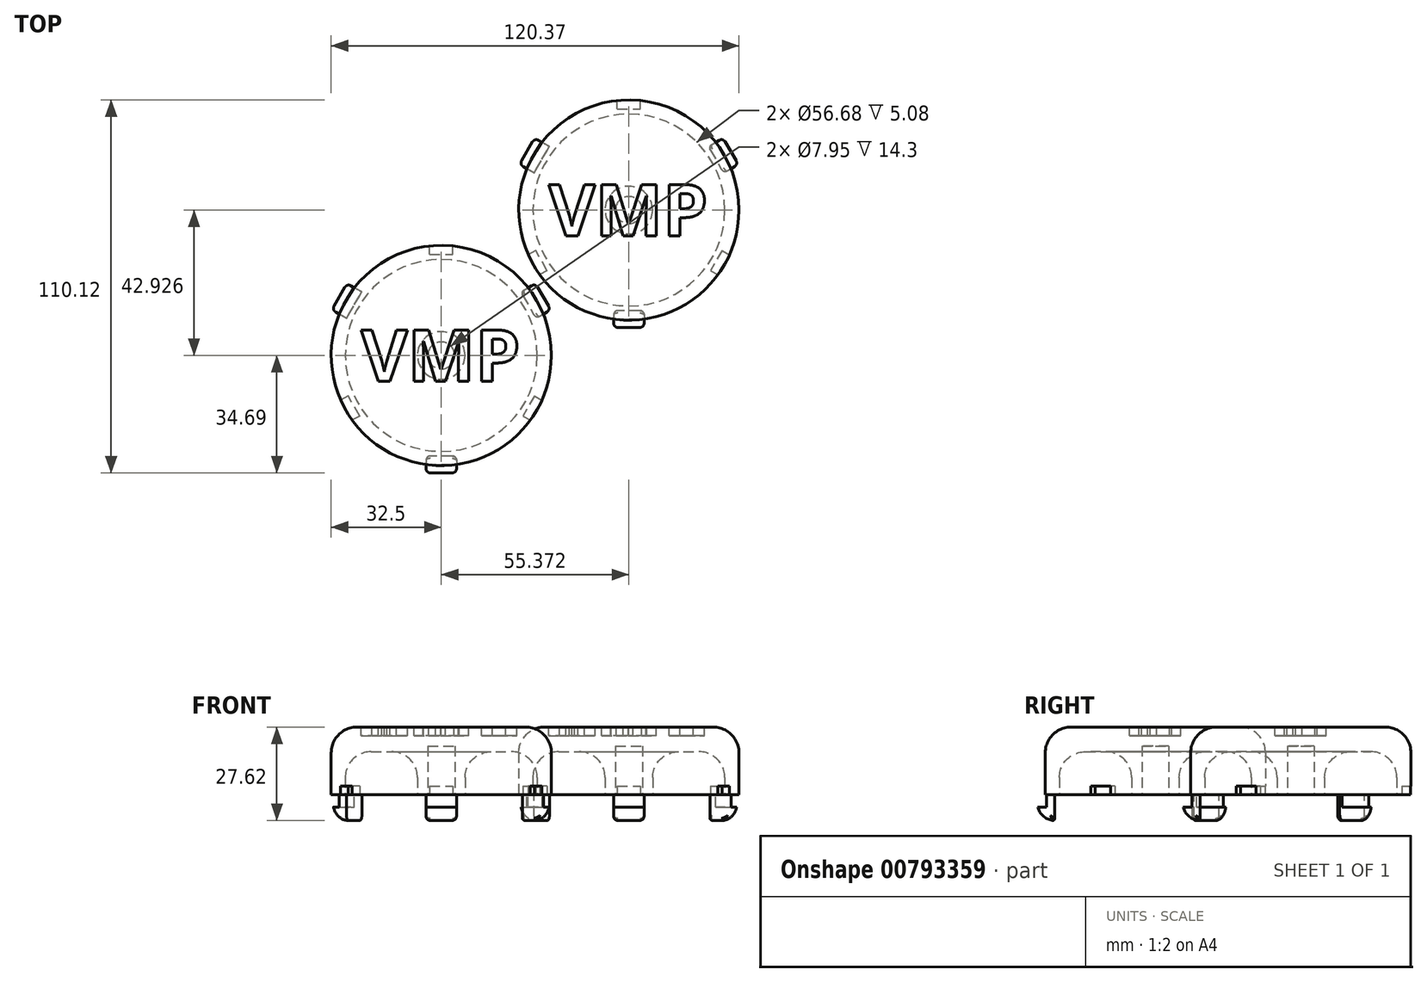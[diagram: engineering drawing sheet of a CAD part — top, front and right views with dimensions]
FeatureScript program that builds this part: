
annotation { "Feature Type Name" : "Feature", "Feature Type Description" : "" }
export const myFeature = defineFeature(function(context is Context, id is Id, definition is map)
    precondition{}
    {
        {
            var Q0;
            Q0=qCreatedBy(makeId("Top.planeOp"),FACE);
            var sketch = newSketch(context, id + "F0", { "sketchPlane" : qUnion([Q0])});
            skCircle(sketch, "E0", {"center": v(0, 0) * mm, "radius": 32.5 * mm});
            skSolve(sketch);
        }
        {
            var Q0;
            Q0=makeQuery(id+"F0.imprint","IMPRINT",FACE,{"disambiguationData":[TD([[makeQuery(id+"F0.imprint","IMPRINT",EDGE,{"derivedFrom":sQuery(id+"F0.wireOp",EDGE,"E0")}),1.0]])]});
            extrude(context, id + "F1", {"entities" : qUnion([Q0]), "depth" : 20 * mm, "offsetDistance" : 25.4 * mm});
        }
        {
            var Q0;
            Q0=makeQuery(id+"F1.opExtrude","CAP_FACE",FACE,{"disambiguationData":[OSD([sQuery(id+"F0.wireOp",EDGE,"E0")])],"isStart":false});
            fillet(context, id + "F2", {"entities" : qUnion([Q0]), "radius" : 7.62 * mm, "tangentPropagation" : true, "allowEdgeOverflow" : false});
        }
        {
            var Q0;
            Q0=makeQuery(id+"F1.opExtrude","CAP_FACE",FACE,{"disambiguationData":[OSD([sQuery(id+"F0.wireOp",EDGE,"E0")])],"isStart":true});
            var sketch = newSketch(context, id + "F3", { "sketchPlane" : qUnion([Q0])});
            skCircle(sketch, "E1", {"center": v(0, 0) * mm, "radius": 3.98 * mm});
            skSolve(sketch);
        }
        {
            var Q0;
            Q0=makeQuery(id+"F3.imprint","IMPRINT",FACE,{"disambiguationData":[TD([[makeQuery(id+"F3.imprint","IMPRINT",EDGE,{"derivedFrom":sQuery(id+"F3.wireOp",EDGE,"E1")}),1.0]])]});
            extrude(context, id + "F4", {"entities" : qUnion([Q0]), "operationType" : NewBodyOperationType.REMOVE, "oppositeDirection" : true, "depth" : 14.3 * mm, "offsetDistance" : 25.4 * mm});
        }
        {
            var Q0;
            Q0=makeQuery(id+"F1.opExtrude","CAP_FACE",FACE,{"disambiguationData":[OSD([sQuery(id+"F0.wireOp",EDGE,"E0")])],"isStart":true});
            var sketch = newSketch(context, id + "F5", { "sketchPlane" : qUnion([Q0])});
            skLineSegment(sketch, "E2.bottom", {"start": v(0, 29.69) * mm, "end": v(-4.5, 29.69) * mm});
            skLineSegment(sketch, "E2.top", {"start": v(0, 32.19) * mm, "end": v(-4.5, 32.19) * mm});
            skLineSegment(sketch, "E2.right", {"start": v(-4.5, 29.69) * mm, "end": v(-4.5, 32.19) * mm});
            skLineSegment(sketch, "E3.MirrorCS", {"start": v(0, 29.69) * mm, "end": v(4.5, 29.69) * mm});
            skLineSegment(sketch, "E4.MirrorCS", {"start": v(4.5, 29.69) * mm, "end": v(4.5, 32.19) * mm});
            skLineSegment(sketch, "E5.MirrorCS", {"start": v(0, 32.19) * mm, "end": v(4.5, 32.19) * mm});
            skLineSegment(sketch, "E6.1.0", {"start": v(-27.87, -16.1) * mm, "end": v(-30.12, -12.2) * mm});
            skLineSegment(sketch, "E6.1.1", {"start": v(-25.7, -14.84) * mm, "end": v(-27.96, -10.95) * mm});
            skLineSegment(sketch, "E6.1.2", {"start": v(-25.7, -14.84) * mm, "end": v(-23.46, -18.74) * mm});
            skLineSegment(sketch, "E6.1.3", {"start": v(-23.46, -18.74) * mm, "end": v(-25.62, -20) * mm});
            skLineSegment(sketch, "E6.1.4", {"start": v(-27.87, -16.1) * mm, "end": v(-25.62, -20) * mm});
            skLineSegment(sketch, "E6.1.5", {"start": v(-27.96, -10.95) * mm, "end": v(-30.12, -12.2) * mm});
            skLineSegment(sketch, "E6.2.0", {"start": v(27.87, -16.1) * mm, "end": v(25.62, -20) * mm});
            skLineSegment(sketch, "E6.2.1", {"start": v(25.7, -14.84) * mm, "end": v(23.46, -18.74) * mm});
            skLineSegment(sketch, "E6.2.2", {"start": v(25.7, -14.84) * mm, "end": v(27.96, -10.95) * mm});
            skLineSegment(sketch, "E6.2.3", {"start": v(27.96, -10.95) * mm, "end": v(30.12, -12.2) * mm});
            skLineSegment(sketch, "E6.2.4", {"start": v(27.87, -16.1) * mm, "end": v(30.12, -12.2) * mm});
            skLineSegment(sketch, "E6.2.5", {"start": v(23.46, -18.74) * mm, "end": v(25.62, -20) * mm});
            skPoint(sketch, "E6.center", {"position": v(0, 0) * mm});
            skSolve(sketch);
        }
        {
            var Q0;
            Q0=makeQuery(id+"F5.imprint","IMPRINT",FACE,{"disambiguationData":[TD([[makeQuery(id+"F5.imprint","IMPRINT",EDGE,{"derivedFrom":sQuery(id+"F5.wireOp",EDGE,"E2.bottom")}),-1.0]])]});
            var Q1;
            Q1=makeQuery(id+"F5.imprint","IMPRINT",FACE,{"disambiguationData":[TD([[makeQuery(id+"F5.imprint","IMPRINT",EDGE,{"derivedFrom":sQuery(id+"F5.wireOp",EDGE,"E6.2.0")}),-1.0]])]});
            var Q2;
            Q2=makeQuery(id+"F5.imprint","IMPRINT",FACE,{"disambiguationData":[TD([[makeQuery(id+"F5.imprint","IMPRINT",EDGE,{"derivedFrom":sQuery(id+"F5.wireOp",EDGE,"E6.1.0")}),-1.0]])]});
            extrude(context, id + "F6", {"entities" : qUnion([Q0, Q1, Q2]), "operationType" : NewBodyOperationType.ADD, "depth" : 7.62 * mm, "offsetDistance" : 25.4 * mm});
        }
        {
            var Q0;
            Q0=makeQuery(id+"F6.opExtrude","SWEPT_FACE",FACE,{"disambiguationData":[OSD([sQuery(id+"F5.wireOp",EDGE,"E6.1.0"),sQuery(id+"F5.wireOp",EDGE,"E6.1.4")])]});
            var sketch = newSketch(context, id + "F7", { "sketchPlane" : qUnion([Q0])});
            skLineSegment(sketch, "E7.bottom", {"start": v(4.5, -7.62) * mm, "end": v(-4.5, -7.62) * mm});
            skLineSegment(sketch, "E7.top", {"start": v(4.5, -3.62) * mm, "end": v(-4.5, -3.62) * mm});
            skLineSegment(sketch, "E7.left", {"start": v(4.5, -7.62) * mm, "end": v(4.5, -3.62) * mm});
            skLineSegment(sketch, "E7.right", {"start": v(-4.5, -7.62) * mm, "end": v(-4.5, -3.62) * mm});
            skSolve(sketch);
        }
        {
            var Q0;
            Q0=makeQuery(id+"F6.opExtrude","SWEPT_FACE",FACE,{"disambiguationData":[OSD([sQuery(id+"F5.wireOp",EDGE,"E6.2.0"),sQuery(id+"F5.wireOp",EDGE,"E6.2.4")])]});
            var sketch = newSketch(context, id + "F8", { "sketchPlane" : qUnion([Q0])});
            skLineSegment(sketch, "E8.bottom", {"start": v(4.5, -7.62) * mm, "end": v(-4.5, -7.62) * mm});
            skLineSegment(sketch, "E8.top", {"start": v(4.5, -3.62) * mm, "end": v(-4.5, -3.62) * mm});
            skLineSegment(sketch, "E8.left", {"start": v(4.5, -7.62) * mm, "end": v(4.5, -3.62) * mm});
            skLineSegment(sketch, "E8.right", {"start": v(-4.5, -7.62) * mm, "end": v(-4.5, -3.62) * mm});
            skSolve(sketch);
        }
        {
            var Q0;
            Q0=makeQuery(id+"F6.opExtrude","SWEPT_FACE",FACE,{"disambiguationData":[OSD([sQuery(id+"F5.wireOp",EDGE,"E2.top"),sQuery(id+"F5.wireOp",EDGE,"E5.MirrorCS")])]});
            var sketch = newSketch(context, id + "F9", { "sketchPlane" : qUnion([Q0])});
            skLineSegment(sketch, "E9.bottom", {"start": v(-4.5, -7.62) * mm, "end": v(4.5, -7.62) * mm});
            skLineSegment(sketch, "E9.top", {"start": v(-4.5, -3.62) * mm, "end": v(4.5, -3.62) * mm});
            skLineSegment(sketch, "E9.left", {"start": v(-4.5, -7.62) * mm, "end": v(-4.5, -3.62) * mm});
            skLineSegment(sketch, "E9.right", {"start": v(4.5, -7.62) * mm, "end": v(4.5, -3.62) * mm});
            skSolve(sketch);
        }
        {
            var Q0;
            Q0=makeQuery(id+"F9.imprint","IMPRINT",FACE,{"disambiguationData":[TD([[makeQuery(id+"F9.imprint","IMPRINT",EDGE,{"derivedFrom":sQuery(id+"F9.wireOp",EDGE,"E9.bottom")}),1.0]])]});
            extrude(context, id + "F10", {"entities" : qUnion([Q0]), "operationType" : NewBodyOperationType.ADD, "depth" : 2.5 * mm, "offsetDistance" : 25.4 * mm});
        }
        {
            var Q0;
            Q0=makeQuery(id+"F7.imprint","IMPRINT",FACE,{"disambiguationData":[TD([[makeQuery(id+"F7.imprint","IMPRINT",EDGE,{"derivedFrom":sQuery(id+"F7.wireOp",EDGE,"E7.bottom")}),1.0]])]});
            extrude(context, id + "F11", {"entities" : qUnion([Q0]), "operationType" : NewBodyOperationType.ADD, "depth" : 2.5 * mm, "offsetDistance" : 25.4 * mm});
        }
        {
            var Q0;
            Q0=makeQuery(id+"F8.imprint","IMPRINT",FACE,{"disambiguationData":[TD([[makeQuery(id+"F8.imprint","IMPRINT",EDGE,{"derivedFrom":sQuery(id+"F8.wireOp",EDGE,"E8.bottom")}),1.0]])]});
            extrude(context, id + "F12", {"entities" : qUnion([Q0]), "operationType" : NewBodyOperationType.ADD, "depth" : 2.5 * mm, "offsetDistance" : 25.4 * mm});
        }
        {
            var Q0;
            Q0=makeQuery(id+"F12.opExtrude","CAP_EDGE",EDGE,{"disambiguationData":[OSD([sQuery(id+"F8.wireOp",EDGE,"E8.bottom")])],"isStart":false});
            var Q1;
            Q1=makeQuery(id+"F10.opExtrude","CAP_EDGE",EDGE,{"disambiguationData":[OSD([sQuery(id+"F9.wireOp",EDGE,"E9.bottom")])],"isStart":false});
            var Q2;
            Q2=makeQuery(id+"F11.opExtrude","CAP_EDGE",EDGE,{"disambiguationData":[OSD([sQuery(id+"F7.wireOp",EDGE,"E7.bottom")])],"isStart":false});
            fillet(context, id + "F13", {"entities" : qUnion([Q0, Q1, Q2]), "radius" : 5.08 * mm, "tangentPropagation" : true, "allowEdgeOverflow" : false});
        }
        {
            var Q0;
            Q0=makeQuery(id+"F6.opExtrude","CAP_EDGE",EDGE,{"disambiguationData":[OSD([sQuery(id+"F5.wireOp",EDGE,"E2.bottom"),sQuery(id+"F5.wireOp",EDGE,"E3.MirrorCS")])],"isStart":false});
            var Q1;
            {var subQ0=sQuery(id+"F7.wireOp",EDGE,"E7.bottom");Q1=makeQuery(id+"F13.opFillet","BLEND_EDGE",EDGE,{"blendedFrom":[makeQuery(id+"F11.opExtrude","CAP_EDGE",EDGE,{"disambiguationData":[OSD([subQ0])],"isStart":false}),makeQuery(id+"F11.boolean.opBoolean","MERGE",FACE,{"derivedFrom":[makeQuery(id+"F6.opExtrude","CAP_FACE",FACE,{"disambiguationData":[OSD([sQuery(id+"F5.wireOp",EDGE,"E6.1.0"),sQuery(id+"F5.wireOp",EDGE,"E6.1.1"),sQuery(id+"F5.wireOp",EDGE,"E6.1.2"),sQuery(id+"F5.wireOp",EDGE,"E6.1.3"),sQuery(id+"F5.wireOp",EDGE,"E6.1.4"),sQuery(id+"F5.wireOp",EDGE,"E6.1.5")])],"isStart":false}),makeQuery(id+"F11.opExtrude","SWEPT_FACE",FACE,{"disambiguationData":[OSD([subQ0])]})]})],"blendedInto":[makeQuery(id+"F11.boolean.opBoolean","MERGE",FACE,{"derivedFrom":[makeQuery(id+"F6.opExtrude","CAP_FACE",FACE,{"disambiguationData":[OSD([sQuery(id+"F5.wireOp",EDGE,"E6.1.0"),sQuery(id+"F5.wireOp",EDGE,"E6.1.1"),sQuery(id+"F5.wireOp",EDGE,"E6.1.2"),sQuery(id+"F5.wireOp",EDGE,"E6.1.3"),sQuery(id+"F5.wireOp",EDGE,"E6.1.4"),sQuery(id+"F5.wireOp",EDGE,"E6.1.5")])],"isStart":false}),makeQuery(id+"F11.opExtrude","SWEPT_FACE",FACE,{"disambiguationData":[OSD([subQ0])]})]})]});}
            var Q2;
            Q2=makeQuery(id+"F6.opExtrude","CAP_EDGE",EDGE,{"disambiguationData":[OSD([sQuery(id+"F5.wireOp",EDGE,"E6.2.1"),sQuery(id+"F5.wireOp",EDGE,"E6.2.2")])],"isStart":false});
            fillet(context, id + "F14", {"entities" : qUnion([Q0, Q1, Q2]), "radius" : 0.64 * mm, "tangentPropagation" : true, "allowEdgeOverflow" : false});
        }
        {
            var Q0;
            Q0=makeQuery(id+"F13.opFillet","BLEND_EDGE",EDGE,{"blendedFrom":[makeQuery(id+"F11.opExtrude","CAP_EDGE",EDGE,{"disambiguationData":[OSD([sQuery(id+"F7.wireOp",EDGE,"E7.bottom")])],"isStart":false}),makeQuery(id+"F11.boolean.opBoolean","MERGE",FACE,{"derivedFrom":[makeQuery(id+"F6.opExtrude","SWEPT_FACE",FACE,{"disambiguationData":[OSD([sQuery(id+"F5.wireOp",EDGE,"E6.1.3")])]}),makeQuery(id+"F11.opExtrude","SWEPT_FACE",FACE,{"disambiguationData":[OSD([sQuery(id+"F7.wireOp",EDGE,"E7.right")])]})]})],"blendedInto":[makeQuery(id+"F11.boolean.opBoolean","MERGE",FACE,{"derivedFrom":[makeQuery(id+"F6.opExtrude","SWEPT_FACE",FACE,{"disambiguationData":[OSD([sQuery(id+"F5.wireOp",EDGE,"E6.1.3")])]}),makeQuery(id+"F11.opExtrude","SWEPT_FACE",FACE,{"disambiguationData":[OSD([sQuery(id+"F7.wireOp",EDGE,"E7.right")])]})]})]});
            var Q1;
            Q1=makeQuery(id+"F13.opFillet","BLEND_EDGE",EDGE,{"blendedFrom":[makeQuery(id+"F11.opExtrude","CAP_EDGE",EDGE,{"disambiguationData":[OSD([sQuery(id+"F7.wireOp",EDGE,"E7.bottom")])],"isStart":false}),makeQuery(id+"F11.boolean.opBoolean","MERGE",FACE,{"derivedFrom":[makeQuery(id+"F6.opExtrude","SWEPT_FACE",FACE,{"disambiguationData":[OSD([sQuery(id+"F5.wireOp",EDGE,"E6.1.5")])]}),makeQuery(id+"F11.opExtrude","SWEPT_FACE",FACE,{"disambiguationData":[OSD([sQuery(id+"F7.wireOp",EDGE,"E7.left")])]})]})],"blendedInto":[makeQuery(id+"F11.boolean.opBoolean","MERGE",FACE,{"derivedFrom":[makeQuery(id+"F6.opExtrude","SWEPT_FACE",FACE,{"disambiguationData":[OSD([sQuery(id+"F5.wireOp",EDGE,"E6.1.5")])]}),makeQuery(id+"F11.opExtrude","SWEPT_FACE",FACE,{"disambiguationData":[OSD([sQuery(id+"F7.wireOp",EDGE,"E7.left")])]})]})]});
            var Q2;
            Q2=makeQuery(id+"F13.opFillet","BLEND_EDGE",EDGE,{"blendedFrom":[makeQuery(id+"F10.opExtrude","CAP_EDGE",EDGE,{"disambiguationData":[OSD([sQuery(id+"F9.wireOp",EDGE,"E9.bottom")])],"isStart":false}),makeQuery(id+"F10.boolean.opBoolean","MERGE",FACE,{"derivedFrom":[makeQuery(id+"F6.opExtrude","SWEPT_FACE",FACE,{"disambiguationData":[OSD([sQuery(id+"F5.wireOp",EDGE,"E2.right")])]}),makeQuery(id+"F10.opExtrude","SWEPT_FACE",FACE,{"disambiguationData":[OSD([sQuery(id+"F9.wireOp",EDGE,"E9.left")])]})]})],"blendedInto":[makeQuery(id+"F10.boolean.opBoolean","MERGE",FACE,{"derivedFrom":[makeQuery(id+"F6.opExtrude","SWEPT_FACE",FACE,{"disambiguationData":[OSD([sQuery(id+"F5.wireOp",EDGE,"E2.right")])]}),makeQuery(id+"F10.opExtrude","SWEPT_FACE",FACE,{"disambiguationData":[OSD([sQuery(id+"F9.wireOp",EDGE,"E9.left")])]})]})]});
            var Q3;
            Q3=makeQuery(id+"F13.opFillet","BLEND_EDGE",EDGE,{"blendedFrom":[makeQuery(id+"F12.opExtrude","CAP_EDGE",EDGE,{"disambiguationData":[OSD([sQuery(id+"F8.wireOp",EDGE,"E8.bottom")])],"isStart":false}),makeQuery(id+"F12.boolean.opBoolean","MERGE",FACE,{"derivedFrom":[makeQuery(id+"F6.opExtrude","SWEPT_FACE",FACE,{"disambiguationData":[OSD([sQuery(id+"F5.wireOp",EDGE,"E6.2.5")])]}),makeQuery(id+"F12.opExtrude","SWEPT_FACE",FACE,{"disambiguationData":[OSD([sQuery(id+"F8.wireOp",EDGE,"E8.left")])]})]})],"blendedInto":[makeQuery(id+"F12.boolean.opBoolean","MERGE",FACE,{"derivedFrom":[makeQuery(id+"F6.opExtrude","SWEPT_FACE",FACE,{"disambiguationData":[OSD([sQuery(id+"F5.wireOp",EDGE,"E6.2.5")])]}),makeQuery(id+"F12.opExtrude","SWEPT_FACE",FACE,{"disambiguationData":[OSD([sQuery(id+"F8.wireOp",EDGE,"E8.left")])]})]})]});
            var Q4;
            Q4=makeQuery(id+"F13.opFillet","BLEND_EDGE",EDGE,{"blendedFrom":[makeQuery(id+"F12.opExtrude","CAP_EDGE",EDGE,{"disambiguationData":[OSD([sQuery(id+"F8.wireOp",EDGE,"E8.bottom")])],"isStart":false}),makeQuery(id+"F12.boolean.opBoolean","MERGE",FACE,{"derivedFrom":[makeQuery(id+"F6.opExtrude","SWEPT_FACE",FACE,{"disambiguationData":[OSD([sQuery(id+"F5.wireOp",EDGE,"E6.2.3")])]}),makeQuery(id+"F12.opExtrude","SWEPT_FACE",FACE,{"disambiguationData":[OSD([sQuery(id+"F8.wireOp",EDGE,"E8.right")])]})]})],"blendedInto":[makeQuery(id+"F12.boolean.opBoolean","MERGE",FACE,{"derivedFrom":[makeQuery(id+"F6.opExtrude","SWEPT_FACE",FACE,{"disambiguationData":[OSD([sQuery(id+"F5.wireOp",EDGE,"E6.2.3")])]}),makeQuery(id+"F12.opExtrude","SWEPT_FACE",FACE,{"disambiguationData":[OSD([sQuery(id+"F8.wireOp",EDGE,"E8.right")])]})]})]});
            var Q5;
            Q5=makeQuery(id+"F13.opFillet","BLEND_EDGE",EDGE,{"blendedFrom":[makeQuery(id+"F10.opExtrude","CAP_EDGE",EDGE,{"disambiguationData":[OSD([sQuery(id+"F9.wireOp",EDGE,"E9.bottom")])],"isStart":false}),makeQuery(id+"F10.boolean.opBoolean","MERGE",FACE,{"derivedFrom":[makeQuery(id+"F6.opExtrude","SWEPT_FACE",FACE,{"disambiguationData":[OSD([sQuery(id+"F5.wireOp",EDGE,"E4.MirrorCS")])]}),makeQuery(id+"F10.opExtrude","SWEPT_FACE",FACE,{"disambiguationData":[OSD([sQuery(id+"F9.wireOp",EDGE,"E9.right")])]})]})],"blendedInto":[makeQuery(id+"F10.boolean.opBoolean","MERGE",FACE,{"derivedFrom":[makeQuery(id+"F6.opExtrude","SWEPT_FACE",FACE,{"disambiguationData":[OSD([sQuery(id+"F5.wireOp",EDGE,"E4.MirrorCS")])]}),makeQuery(id+"F10.opExtrude","SWEPT_FACE",FACE,{"disambiguationData":[OSD([sQuery(id+"F9.wireOp",EDGE,"E9.right")])]})]})]});
            fillet(context, id + "F15", {"entities" : qUnion([Q0, Q1, Q2, Q3, Q4, Q5]), "radius" : 1.27 * mm, "tangentPropagation" : true, "allowEdgeOverflow" : false});
        }
        {
            var Q0;
            {var subQ0=sQuery(id+"F0.wireOp",EDGE,"E0");var subQ1=makeQuery(id+"F1.opExtrude","CAP_FACE",FACE,{"disambiguationData":[OSD([subQ0])],"isStart":true});Q0=makeQuery(id+"F6.boolean.opBoolean","SPLIT",FACE,{"disambiguationData":[TD([makeQuery(id+"F1.opExtrude","SWEPT_FACE",FACE,{"disambiguationData":[OSD([subQ0])]}),subQ1,makeQuery(id+"F4.boolean.opBoolean","COPY",FACE,{"derivedFrom":makeQuery(id+"F4.opExtrude","SWEPT_FACE",FACE,{"disambiguationData":[OSD([sQuery(id+"F3.wireOp",EDGE,"E1")])]})}),makeQuery(id+"F6.opExtrude","SWEPT_FACE",FACE,{"disambiguationData":[OSD([sQuery(id+"F5.wireOp",EDGE,"E2.bottom"),sQuery(id+"F5.wireOp",EDGE,"E3.MirrorCS")])]}),makeQuery(id+"F6.opExtrude","SWEPT_FACE",FACE,{"disambiguationData":[OSD([sQuery(id+"F5.wireOp",EDGE,"E2.top"),sQuery(id+"F5.wireOp",EDGE,"E5.MirrorCS")])]}),makeQuery(id+"F6.opExtrude","SWEPT_FACE",FACE,{"disambiguationData":[OSD([sQuery(id+"F5.wireOp",EDGE,"E2.right")])]}),makeQuery(id+"F6.opExtrude","SWEPT_FACE",FACE,{"disambiguationData":[OSD([sQuery(id+"F5.wireOp",EDGE,"E4.MirrorCS")])]}),makeQuery(id+"F6.opExtrude","SWEPT_FACE",FACE,{"disambiguationData":[OSD([sQuery(id+"F5.wireOp",EDGE,"E6.1.0"),sQuery(id+"F5.wireOp",EDGE,"E6.1.4")])]}),makeQuery(id+"F6.opExtrude","SWEPT_FACE",FACE,{"disambiguationData":[OSD([sQuery(id+"F5.wireOp",EDGE,"E6.1.1"),sQuery(id+"F5.wireOp",EDGE,"E6.1.2")])]}),makeQuery(id+"F6.opExtrude","SWEPT_FACE",FACE,{"disambiguationData":[OSD([sQuery(id+"F5.wireOp",EDGE,"E6.1.3")])]}),makeQuery(id+"F6.opExtrude","SWEPT_FACE",FACE,{"disambiguationData":[OSD([sQuery(id+"F5.wireOp",EDGE,"E6.1.5")])]}),makeQuery(id+"F6.opExtrude","SWEPT_FACE",FACE,{"disambiguationData":[OSD([sQuery(id+"F5.wireOp",EDGE,"E6.2.0"),sQuery(id+"F5.wireOp",EDGE,"E6.2.4")])]}),makeQuery(id+"F6.opExtrude","SWEPT_FACE",FACE,{"disambiguationData":[OSD([sQuery(id+"F5.wireOp",EDGE,"E6.2.1"),sQuery(id+"F5.wireOp",EDGE,"E6.2.2")])]}),makeQuery(id+"F6.opExtrude","SWEPT_FACE",FACE,{"disambiguationData":[OSD([sQuery(id+"F5.wireOp",EDGE,"E6.2.3")])]}),makeQuery(id+"F6.opExtrude","SWEPT_FACE",FACE,{"disambiguationData":[OSD([sQuery(id+"F5.wireOp",EDGE,"E6.2.5")])]})])],"derivedFrom":subQ1});}
            var sketch = newSketch(context, id + "F16", { "sketchPlane" : qUnion([Q0])});
            skCircle(sketch, "E10", {"center": v(0, 0) * mm, "radius": 7.02 * mm});
            skCircle(sketch, "E11", {"center": v(0, 0) * mm, "radius": 28.34 * mm});
            skSolve(sketch);
        }
        {
            var Q0;
            Q0=makeQuery(id+"F16.imprint","IMPRINT",FACE,{"disambiguationData":[TD([[makeQuery(id+"F16.imprint","IMPRINT",EDGE,{"derivedFrom":sQuery(id+"F16.wireOp",EDGE,"E10")}),-1.0]])]});
            extrude(context, id + "F17", {"entities" : qUnion([Q0]), "operationType" : NewBodyOperationType.REMOVE, "oppositeDirection" : true, "depth" : 12.7 * mm, "offsetDistance" : 25.4 * mm});
        }
        {
            var Q0;
            Q0=makeQuery(id+"F17.boolean.opBoolean","COPY",EDGE,{"derivedFrom":makeQuery(id+"F17.opExtrude","CAP_EDGE",EDGE,{"disambiguationData":[OSD([sQuery(id+"F16.wireOp",EDGE,"E11")])],"isStart":false})});
            var Q1;
            Q1=makeQuery(id+"F17.boolean.opBoolean","COPY",EDGE,{"derivedFrom":makeQuery(id+"F17.opExtrude","CAP_EDGE",EDGE,{"disambiguationData":[OSD([sQuery(id+"F16.wireOp",EDGE,"E10")])],"isStart":false})});
            fillet(context, id + "F18", {"entities" : qUnion([Q0, Q1]), "radius" : 7.62 * mm, "tangentPropagation" : true, "allowEdgeOverflow" : false});
        }
        {
            var Q0;
            {var subQ0=sQuery(id+"F5.wireOp",EDGE,"E6.2.3");var subQ1=makeQuery(id+"F6.opExtrude","SWEPT_FACE",FACE,{"disambiguationData":[OSD([subQ0])]});var subQ2=sQuery(id+"F5.wireOp",EDGE,"E6.2.5");var subQ3=makeQuery(id+"F6.opExtrude","SWEPT_FACE",FACE,{"disambiguationData":[OSD([subQ2])]});var subQ4=sQuery(id+"F5.wireOp",EDGE,"E6.2.2");var subQ5=sQuery(id+"F5.wireOp",EDGE,"E6.2.1");var subQ6=makeQuery(id+"F6.opExtrude","SWEPT_FACE",FACE,{"disambiguationData":[OSD([subQ5,subQ4])]});var subQ7=makeQuery(id+"F6.opExtrude","SWEPT_FACE",FACE,{"disambiguationData":[OSD([sQuery(id+"F5.wireOp",EDGE,"E6.2.0"),sQuery(id+"F5.wireOp",EDGE,"E6.2.4")])]});var subQ8=makeQuery(id+"F6.opExtrude","SWEPT_FACE",FACE,{"disambiguationData":[OSD([sQuery(id+"F5.wireOp",EDGE,"E2.top"),sQuery(id+"F5.wireOp",EDGE,"E5.MirrorCS")])]});var subQ9=sQuery(id+"F0.wireOp",EDGE,"E0");var subQ10=makeQuery(id+"F1.opExtrude","CAP_FACE",FACE,{"disambiguationData":[OSD([subQ9])],"isStart":true});var subQ11=sQuery(id+"F5.wireOp",EDGE,"E3.MirrorCS");var subQ12=sQuery(id+"F5.wireOp",EDGE,"E2.bottom");var subQ13=makeQuery(id+"F6.opExtrude","SWEPT_FACE",FACE,{"disambiguationData":[OSD([subQ12,subQ11])]});var subQ14=makeQuery(id+"F1.opExtrude","SWEPT_FACE",FACE,{"disambiguationData":[OSD([subQ9])]});var subQ15=sQuery(id+"F5.wireOp",EDGE,"E2.right");var subQ16=makeQuery(id+"F6.opExtrude","SWEPT_FACE",FACE,{"disambiguationData":[OSD([subQ15])]});var subQ17=sQuery(id+"F5.wireOp",EDGE,"E4.MirrorCS");var subQ18=makeQuery(id+"F6.opExtrude","SWEPT_FACE",FACE,{"disambiguationData":[OSD([subQ17])]});var subQ19=makeQuery(id+"F6.opExtrude","SWEPT_FACE",FACE,{"disambiguationData":[OSD([sQuery(id+"F5.wireOp",EDGE,"E6.1.0"),sQuery(id+"F5.wireOp",EDGE,"E6.1.4")])]});var subQ20=makeQuery(id+"F6.opExtrude","SWEPT_FACE",FACE,{"disambiguationData":[OSD([sQuery(id+"F5.wireOp",EDGE,"E6.1.1"),sQuery(id+"F5.wireOp",EDGE,"E6.1.2")])]});var subQ21=makeQuery(id+"F6.opExtrude","SWEPT_FACE",FACE,{"disambiguationData":[OSD([sQuery(id+"F5.wireOp",EDGE,"E6.1.3")])]});var subQ22=makeQuery(id+"F6.opExtrude","SWEPT_FACE",FACE,{"disambiguationData":[OSD([sQuery(id+"F5.wireOp",EDGE,"E6.1.5")])]});Q0=makeQuery(id+"F17.boolean.opBoolean","SPLIT",FACE,{"disambiguationData":[TD([subQ14])],"derivedFrom":makeQuery(id+"F6.boolean.opBoolean","SPLIT",FACE,{"disambiguationData":[TD([subQ14,subQ10,makeQuery(id+"F4.boolean.opBoolean","COPY",FACE,{"derivedFrom":makeQuery(id+"F4.opExtrude","SWEPT_FACE",FACE,{"disambiguationData":[OSD([sQuery(id+"F3.wireOp",EDGE,"E1")])]})}),subQ13,subQ8,subQ16,subQ18,subQ19,subQ20,subQ21,subQ22,subQ7,subQ6,subQ1,subQ3])],"derivedFrom":subQ10})});}
            var sketch = newSketch(context, id + "F19", { "sketchPlane" : qUnion([Q0])});
            skLineSegment(sketch, "E12.bottom", {"start": v(-3.42, -29.8) * mm, "end": v(3.42, -29.8) * mm});
            skLineSegment(sketch, "E12.top", {"start": v(-3.42, -35.2) * mm, "end": v(3.42, -35.2) * mm});
            skLineSegment(sketch, "E12.left", {"start": v(-3.42, -29.8) * mm, "end": v(-3.42, -35.2) * mm});
            skLineSegment(sketch, "E12.right", {"start": v(3.42, -29.8) * mm, "end": v(3.42, -35.2) * mm});
            skPoint(sketch, "E12.middle", {"position": v(0, -32.5) * mm});
            skLineSegment(sketch, "E13.1.0", {"start": v(32.2, 14.64) * mm, "end": v(28.78, 20.56) * mm});
            skLineSegment(sketch, "E13.1.1", {"start": v(27.52, 11.94) * mm, "end": v(32.2, 14.64) * mm});
            skLineSegment(sketch, "E13.1.2", {"start": v(27.52, 11.94) * mm, "end": v(24.1, 17.86) * mm});
            skLineSegment(sketch, "E13.1.3", {"start": v(24.1, 17.86) * mm, "end": v(28.78, 20.56) * mm});
            skLineSegment(sketch, "E13.2.0", {"start": v(-28.78, 20.56) * mm, "end": v(-32.2, 14.64) * mm});
            skLineSegment(sketch, "E13.2.1", {"start": v(-24.1, 17.86) * mm, "end": v(-28.78, 20.56) * mm});
            skLineSegment(sketch, "E13.2.2", {"start": v(-24.1, 17.86) * mm, "end": v(-27.52, 11.94) * mm});
            skLineSegment(sketch, "E13.2.3", {"start": v(-27.52, 11.94) * mm, "end": v(-32.2, 14.64) * mm});
            skPoint(sketch, "E13.center", {"position": v(0, 0) * mm});
            skSolve(sketch);
        }
        {
            var Q0;
            {var subQ0=sQuery(id+"F19.wireOp",EDGE,"E12.top");Q0=makeQuery(id+"F19.imprint","IMPRINT",FACE,{"disambiguationData":[TD([[makeQuery(id+"F19.imprint","IMPRINT",EDGE,{"derivedFrom":subQ0}),1.0]])]});}
            var Q1;
            {var subQ0=sQuery(id+"F19.wireOp",EDGE,"E12.bottom");Q1=makeQuery(id+"F19.imprint","IMPRINT",FACE,{"disambiguationData":[TD([[makeQuery(id+"F19.imprint","IMPRINT",EDGE,{"derivedFrom":subQ0}),-1.0]])]});}
            var Q2;
            {var subQ0=sQuery(id+"F19.wireOp",EDGE,"E13.2.0");Q2=makeQuery(id+"F19.imprint","IMPRINT",FACE,{"disambiguationData":[TD([[makeQuery(id+"F19.imprint","IMPRINT",EDGE,{"derivedFrom":subQ0}),1.0]])]});}
            var Q3;
            {var subQ0=sQuery(id+"F19.wireOp",EDGE,"E13.2.2");Q3=makeQuery(id+"F19.imprint","IMPRINT",FACE,{"disambiguationData":[TD([[makeQuery(id+"F19.imprint","IMPRINT",EDGE,{"derivedFrom":subQ0}),-1.0]])]});}
            var Q4;
            {var subQ0=sQuery(id+"F19.wireOp",EDGE,"E13.1.0");Q4=makeQuery(id+"F19.imprint","IMPRINT",FACE,{"disambiguationData":[TD([[makeQuery(id+"F19.imprint","IMPRINT",EDGE,{"derivedFrom":subQ0}),1.0]])]});}
            var Q5;
            {var subQ0=sQuery(id+"F19.wireOp",EDGE,"E13.1.2");Q5=makeQuery(id+"F19.imprint","IMPRINT",FACE,{"disambiguationData":[TD([[makeQuery(id+"F19.imprint","IMPRINT",EDGE,{"derivedFrom":subQ0}),-1.0]])]});}
            extrude(context, id + "F20", {"entities" : qUnion([Q0, Q1, Q2, Q3, Q4, Q5]), "operationType" : NewBodyOperationType.REMOVE, "oppositeDirection" : true, "depth" : 2.54 * mm, "offsetDistance" : 25.4 * mm});
        }
        {
            var Q0;
            Q0=makeQuery(id+"F1.opExtrude","CAP_FACE",FACE,{"disambiguationData":[OSD([sQuery(id+"F0.wireOp",EDGE,"E0")])],"isStart":false});
            var sketch = newSketch(context, id + "F21", { "sketchPlane" : qUnion([Q0])});
            skText(sketch, "E14", { "text": "VMP", "fontName": "OpenSans-Bold.ttf"});
            const initialGuessF21  = {"E14": [-0.02369, -0.00761, 1, 0, 0.01522]};
            skSetInitialGuess(sketch, initialGuessF21);
            skSolve(sketch);
        }
        {
            var Q0;
            Q0=makeQuery(id+"F21.imprint","IMPRINT",FACE,{"disambiguationData":[TD([[makeQuery(id+"F21.imprint","IMPRINT",EDGE,{"derivedFrom":sQuery(id+"F21.wireOp",EDGE,"E14.sketch_text.stroke-10")}),-1.0]])]});
            var Q1;
            Q1=makeQuery(id+"F21.imprint","IMPRINT",FACE,{"disambiguationData":[TD([[makeQuery(id+"F21.imprint","IMPRINT",EDGE,{"derivedFrom":sQuery(id+"F21.wireOp",EDGE,"E14.sketch_text.stroke-0")}),-1.0]])]});
            var Q2;
            Q2=makeQuery(id+"F21.imprint","IMPRINT",FACE,{"disambiguationData":[TD([[makeQuery(id+"F21.imprint","IMPRINT",EDGE,{"derivedFrom":sQuery(id+"F21.wireOp",EDGE,"E14.sketch_text.stroke-29")}),-1.0]])]});
            extrude(context, id + "F22", {"entities" : qUnion([Q0, Q1, Q2]), "operationType" : NewBodyOperationType.REMOVE, "oppositeDirection" : true, "depth" : 2.54 * mm, "offsetDistance" : 25.4 * mm});
        }
        {
            var Q0;
            Q0=makeQuery(id+"F1.opExtrude","SWEPT_BODY",BODY,{"disambiguationData":[OSD([sQuery(id+"F0.wireOp",EDGE,"E0")])]});
            transform(context, id + "F23", {"entities" : qUnion([Q0]), "transformType" : TransformType.TRANSLATION_3D, "dx" : 55.37 * mm, "dy" : 42.93 * mm, "dz" : 0 * mm, "makeCopy" : true});
        }
    });
